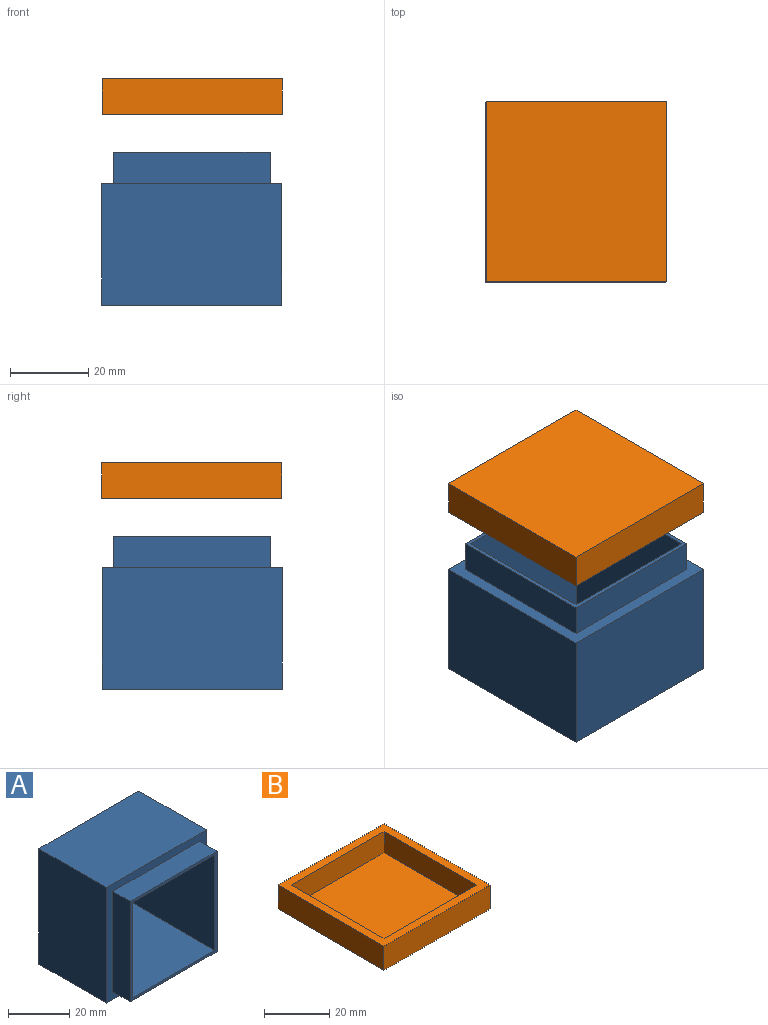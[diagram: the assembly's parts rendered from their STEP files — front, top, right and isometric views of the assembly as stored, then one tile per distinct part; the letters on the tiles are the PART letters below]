
ASSEMBLY  parts=2 mates=1
PART A: 16 faces, bbox 46x39x46 mm
  f0: plane 46x31mm, normal (0,0,-1), area 1426mm2, adj f1,f3,f4,f5
  f1: plane 46x31mm, normal (1,0,0), area 1426mm2, adj f0,f2,f4,f5
  f2: plane 46x31mm, normal (0,0,1), area 1426mm2, adj f1,f3,f4,f5
  f3: plane 46x31mm, normal (-1,0,0), area 1426mm2, adj f0,f2,f4,f5
  f4: plane 46x46mm, normal (0,-1,0), area 516mm2, adj f0,f1,f2,f3,f6,f7,f8,f13
  f5: plane 46x46mm, normal (0,1,0), area 2116mm2, adj f0,f1,f2,f3
  f6: plane 40x8mm, normal (0,0,-1), area 320mm2, adj f4,f7,f13,f14
  f7: plane 40x8mm, normal (1,0,0), area 320mm2, adj f4,f6,f8,f14
  f8: plane 40x8mm, normal (0,0,1), area 320mm2, adj f4,f7,f13,f14
  f9: plane 38x38mm, normal (-1,0,0), area 1444mm2, adj f10,f12,f14,f15
  f10: plane 38x38mm, normal (0,0,1), area 1444mm2, adj f9,f11,f14,f15
  f11: plane 38x38mm, normal (1,0,0), area 1444mm2, adj f10,f12,f14,f15
  f12: plane 38x38mm, normal (0,0,-1), area 1444mm2, adj f9,f11,f14,f15
  f13: plane 40x8mm, normal (-1,0,0), area 320mm2, adj f4,f6,f8,f14
  f14: plane 40x40mm, normal (0,-1,0), area 156mm2, adj f6,f7,f8,f9,f10,f11,f12,f13
  f15: plane 38x38mm, normal (0,-1,0), area 1444mm2, adj f9,f10,f11,f12
PART B: 11 faces, bbox 46x46x9 mm
  f0: plane 46x46mm, normal (0,0,-1), area 2116mm2, adj f5,f6,f7,f8
  f1: plane 40.2x8mm, normal (0,1,0), area 321.6mm2, adj f2,f4,f9,f10
  f2: plane 40.2x8mm, normal (-1,0,0), area 321.6mm2, adj f1,f3,f9,f10
  f3: plane 40.2x8mm, normal (0,-1,0), area 321.6mm2, adj f2,f4,f9,f10
  f4: plane 40.2x8mm, normal (1,0,0), area 321.6mm2, adj f1,f3,f9,f10
  f5: plane 46x9mm, normal (0,-1,0), area 414mm2, adj f0,f6,f8,f9
  f6: plane 46x9mm, normal (1,0,0), area 414mm2, adj f0,f5,f7,f9
  f7: plane 46x9mm, normal (0,1,0), area 414mm2, adj f0,f6,f8,f9
  f8: plane 46x9mm, normal (-1,0,0), area 414mm2, adj f0,f5,f7,f9
  f9: plane 46x46mm, normal (0,0,1), area 500mm2, adj f1,f2,f3,f4,f5,f6,f7,f8
  f10: plane 40.2x40.2mm, normal (0,0,1), area 1616mm2, adj f1,f2,f3,f4
PLACE A rot(axis=(-1,0,0),90deg) t=(-19.49,19.83,-36.97)mm fixed
PLACE B rot(axis=(-1,0,0),180deg) t=(-19.39,19.93,20.8)mm
MATE slider B.f9 <-> A.f14  axis (0,0,-1) through (-39.49,-0.17,11.8)mm
